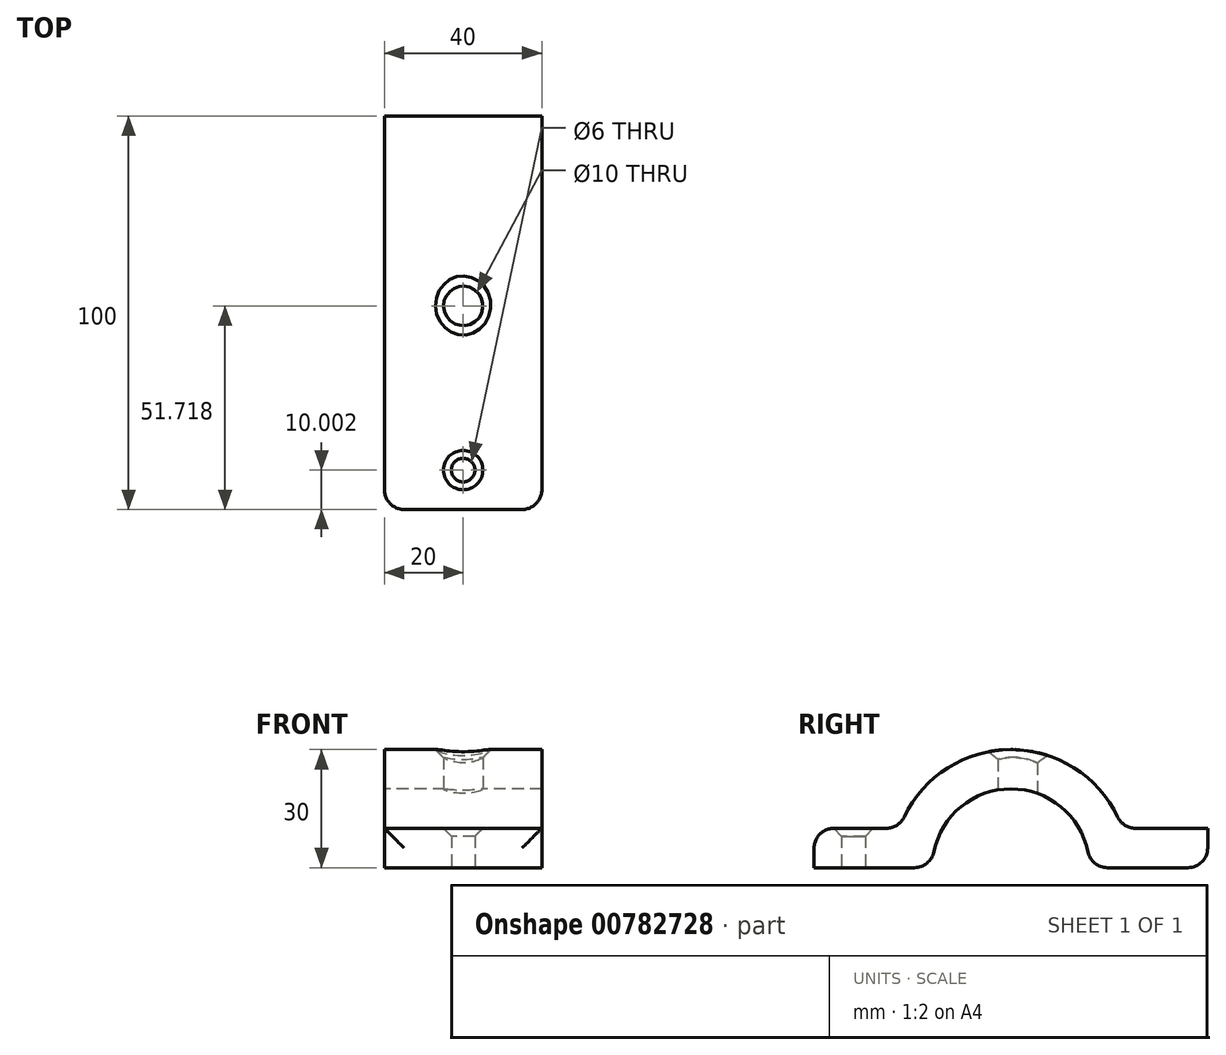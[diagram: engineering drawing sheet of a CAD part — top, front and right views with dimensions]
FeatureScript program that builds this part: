
annotation { "Feature Type Name" : "Feature", "Feature Type Description" : "" }
export const myFeature = defineFeature(function(context is Context, id is Id, definition is map)
    precondition{}
    {
        {
            var Q0;
            Q0=qCreatedBy(makeId("Right.planeOp"),FACE);
            var sketch = newSketch(context, id + "F0", { "sketchPlane" : qUnion([Q0])});
            skLineSegment(sketch, "E0.bottom", {"start": v(-60.57, 10) * mm, "end": v(39.43, 10) * mm});
            skLineSegment(sketch, "E0.top", {"start": v(-60.57, 0) * mm, "end": v(39.43, 0) * mm});
            skLineSegment(sketch, "E0.left", {"start": v(-60.57, 10) * mm, "end": v(-60.57, 0) * mm});
            skLineSegment(sketch, "E0.right", {"start": v(39.43, 10) * mm, "end": v(39.43, 0) * mm});
            skLineSegment(sketch, "E1.bottom", {"start": v(39.43, 10) * mm, "end": v(26.15, 10) * mm});
            skLineSegment(sketch, "E1.top", {"start": v(39.43, 50) * mm, "end": v(26.15, 50) * mm});
            skLineSegment(sketch, "E1.left", {"start": v(39.43, 10) * mm, "end": v(39.43, 50) * mm});
            skLineSegment(sketch, "E1.right", {"start": v(26.15, 10) * mm, "end": v(26.15, 50) * mm});
            skPoint(sketch, "E2", {"position": v(-10.57, 0) * mm});
            skCircle(sketch, "E3", {"center": v(-10.57, 0) * mm, "radius": 30 * mm});
            skCircle(sketch, "E4", {"center": v(-10.57, 0) * mm, "radius": 20 * mm});
            skSolve(sketch);
        }
        {
            var Q0;
            {var subQ0=sQuery(id+"F0.wireOp",EDGE,"E0.left");Q0=makeQuery(id+"F0.imprint","IMPRINT",FACE,{"disambiguationData":[TD([[makeQuery(id+"F0.imprint","IMPRINT",EDGE,{"derivedFrom":subQ0}),1.0]])]});}
            var Q1;
            {var subQ0=sQuery(id+"F0.wireOp",EDGE,"E3");var subQ1=sQuery(id+"F0.wireOp",EDGE,"E0.bottom");var subQ2=makeQuery(id+"F0.imprint","INTERSECT",VERTEX,{"disambiguationData":[OD(0.0)],"derivedFrom":[subQ1,subQ0]});Q1=makeQuery(id+"F0.imprint","IMPRINT",FACE,{"disambiguationData":[TD([[makeQuery(id+"F0.imprint","IMPRINT",EDGE,{"disambiguationData":[TD([[subQ2,-1.0]])],"derivedFrom":subQ1}),-1.0]])]});}
            var Q2;
            {var subQ0=sQuery(id+"F0.wireOp",EDGE,"E3");var subQ1=sQuery(id+"F0.wireOp",EDGE,"E0.bottom");var subQ2=makeQuery(id+"F0.imprint","INTERSECT",VERTEX,{"disambiguationData":[OD(0.0)],"derivedFrom":[subQ1,subQ0]});Q2=makeQuery(id+"F0.imprint","IMPRINT",FACE,{"disambiguationData":[TD([[makeQuery(id+"F0.imprint","IMPRINT",EDGE,{"disambiguationData":[TD([[subQ2,-1.0]])],"derivedFrom":subQ1}),1.0]])]});}
            var Q3;
            {var subQ0=sQuery(id+"F0.wireOp",EDGE,"E3");var subQ1=sQuery(id+"F0.wireOp",EDGE,"E0.bottom");var subQ2=makeQuery(id+"F0.imprint","INTERSECT",VERTEX,{"disambiguationData":[OD(1.0)],"derivedFrom":[subQ1,subQ0]});Q3=makeQuery(id+"F0.imprint","IMPRINT",FACE,{"disambiguationData":[TD([[makeQuery(id+"F0.imprint","IMPRINT",EDGE,{"disambiguationData":[TD([[subQ2,1.0]])],"derivedFrom":subQ1}),-1.0]])]});}
            var Q4;
            {var subQ1=sQuery(id+"F0.wireOp",EDGE,"E0.right");Q4=makeQuery(id+"F0.imprint","IMPRINT",FACE,{"disambiguationData":[TD([[makeQuery(id+"F0.imprint","IMPRINT",EDGE,{"derivedFrom":subQ1}),-1.0]])]});}
            var Q5;
            Q5=makeQuery(id+"F0.imprint","IMPRINT",FACE,{"disambiguationData":[TD([[makeQuery(id+"F0.imprint","IMPRINT",EDGE,{"derivedFrom":sQuery(id+"F0.wireOp",EDGE,"E1.bottom")}),-1.0]])]});
            extrude(context, id + "F1", {"entities" : qUnion([Q0, Q1, Q2, Q3, Q4, Q5]), "endBound" : BoundingType.SYMMETRIC, "depth" : 40 * mm, "offsetDistance" : 25 * mm});
        }
        {
            var Q0;
            Q0=makeQuery(id+"F1.opExtrude","SWEPT_FACE",FACE,{"disambiguationData":[OSD([sQuery(id+"F0.wireOp",EDGE,"E0.right"),sQuery(id+"F0.wireOp",EDGE,"E1.left")])]});
            var sketch = newSketch(context, id + "F2", { "sketchPlane" : qUnion([Q0])});
            skLineSegment(sketch, "E5.bottom", {"start": v(-5, 50) * mm, "end": v(5, 50) * mm});
            skLineSegment(sketch, "E5.top", {"start": v(-3, 35) * mm, "end": v(3, 35) * mm});
            skLineSegment(sketch, "E5.left", {"start": v(-5, 50) * mm, "end": v(-5, 37) * mm});
            skLineSegment(sketch, "E5.right", {"start": v(5, 50) * mm, "end": v(5, 37) * mm});
            skPoint(sketch, "E6.visualSharp", {"position": v(5, 35) * mm});
            skArc(sketch, "E6.filletArc", {"start": v(3, 35) * mm, "mid": v(4.41, 35.59) * mm, "end": v(5, 37) * mm});
            skPoint(sketch, "E7.visualSharp", {"position": v(-5, 35) * mm});
            skArc(sketch, "E7.filletArc", {"start": v(-5, 37) * mm, "mid": v(-4.41, 35.59) * mm, "end": v(-3, 35) * mm});
            skPoint(sketch, "E8", {"position": v(0, 50) * mm});
            skPoint(sketch, "E9", {"position": v(0, 25) * mm});
            skCircle(sketch, "E10", {"center": v(0, 25) * mm, "radius": 3 * mm});
            skSolve(sketch);
        }
        {
            var Q0;
            Q0=makeQuery(id+"F2.imprint","IMPRINT",FACE,{"disambiguationData":[TD([[makeQuery(id+"F2.imprint","IMPRINT",EDGE,{"derivedFrom":sQuery(id+"F2.wireOp",EDGE,"E5.bottom")}),-1.0]])]});
            extrude(context, id + "F3", {"entities" : qUnion([Q0]), "operationType" : NewBodyOperationType.REMOVE, "oppositeDirection" : true, "depth" : 15.6 * mm, "offsetDistance" : 25 * mm});
        }
        {
            var Q0;
            Q0=qCreatedBy(makeId("Top.planeOp"),FACE);
            var sketch = newSketch(context, id + "F4", { "sketchPlane" : qUnion([Q0])});
            skCircle(sketch, "E11", {"center": v(0, -50.57) * mm, "radius": 3 * mm});
            skCircle(sketch, "E12", {"center": v(0, -8.85) * mm, "radius": 5 * mm});
            skSolve(sketch);
        }
        {
            var Q0;
            Q0=makeQuery(id+"F4.imprint","IMPRINT",FACE,{"disambiguationData":[TD([[makeQuery(id+"F4.imprint","IMPRINT",EDGE,{"derivedFrom":sQuery(id+"F4.wireOp",EDGE,"E11")}),1.0]])]});
            var Q1;
            Q1=makeQuery(id+"F4.imprint","IMPRINT",FACE,{"disambiguationData":[TD([[makeQuery(id+"F4.imprint","IMPRINT",EDGE,{"derivedFrom":sQuery(id+"F4.wireOp",EDGE,"E12")}),1.0]])]});
            extrude(context, id + "F5", {"entities" : qUnion([Q0, Q1]), "operationType" : NewBodyOperationType.REMOVE, "depth" : 34.2 * mm, "offsetDistance" : 25 * mm});
        }
        {
            var Q0;
            Q0=makeQuery(id+"F1.opExtrude","CAP_EDGE",EDGE,{"disambiguationData":[OSD([sQuery(id+"F0.wireOp",EDGE,"E1.top")])],"isStart":true});
            var Q1;
            Q1=makeQuery(id+"F1.opExtrude","CAP_EDGE",EDGE,{"disambiguationData":[OSD([sQuery(id+"F0.wireOp",EDGE,"E1.top")])],"isStart":false});
            var Q2;
            Q2=makeQuery(id+"F1.opExtrude","CAP_EDGE",EDGE,{"disambiguationData":[OSD([sQuery(id+"F0.wireOp",EDGE,"E0.left")])],"isStart":false});
            var Q3;
            Q3=makeQuery(id+"F1.opExtrude","CAP_EDGE",EDGE,{"disambiguationData":[OSD([sQuery(id+"F0.wireOp",EDGE,"E0.left")])],"isStart":true});
            var Q4;
            {var subQ0=sQuery(id+"F0.wireOp",EDGE,"E4");var subQ1=sQuery(id+"F0.wireOp",EDGE,"E0.top");Q4=makeQuery(id+"F1.opExtrude","SWEPT_EDGE",EDGE,{"disambiguationData":[OSD([subQ1,subQ0]),TDD([makeQuery(id+"F0.imprint","INTERSECT",VERTEX,{"disambiguationData":[OD(1.0)],"derivedFrom":[subQ1,subQ0]})])]});}
            var Q5;
            {var subQ0=sQuery(id+"F0.wireOp",EDGE,"E4");var subQ1=sQuery(id+"F0.wireOp",EDGE,"E0.top");Q5=makeQuery(id+"F1.opExtrude","SWEPT_EDGE",EDGE,{"disambiguationData":[OSD([subQ1,subQ0]),TDD([makeQuery(id+"F0.imprint","INTERSECT",VERTEX,{"disambiguationData":[OD(0.0)],"derivedFrom":[subQ1,subQ0]})])]});}
            var Q6;
            {var subQ0=sQuery(id+"F0.wireOp",EDGE,"E3");var subQ1=sQuery(id+"F0.wireOp",EDGE,"E0.bottom");Q6=makeQuery(id+"F1.opExtrude","SWEPT_EDGE",EDGE,{"disambiguationData":[OSD([subQ1,subQ0]),TDD([makeQuery(id+"F0.imprint","INTERSECT",VERTEX,{"disambiguationData":[OD(0.0)],"derivedFrom":[subQ1,subQ0]})])]});}
            var Q7;
            {var subQ0=sQuery(id+"F0.wireOp",EDGE,"E3");var subQ1=sQuery(id+"F0.wireOp",EDGE,"E0.bottom");Q7=makeQuery(id+"F1.opExtrude","SWEPT_EDGE",EDGE,{"disambiguationData":[OSD([subQ1,subQ0]),TDD([makeQuery(id+"F0.imprint","INTERSECT",VERTEX,{"disambiguationData":[OD(1.0)],"derivedFrom":[subQ1,subQ0]})])]});}
            var Q8;
            Q8=makeQuery(id+"F1.opExtrude","SWEPT_EDGE",EDGE,{"disambiguationData":[OSD([sQuery(id+"F0.wireOp",EDGE,"E0.bottom"),sQuery(id+"F0.wireOp",EDGE,"E1.bottom"),sQuery(id+"F0.wireOp",EDGE,"E1.right")])]});
            var Q9;
            Q9=makeQuery(id+"F1.opExtrude","SWEPT_EDGE",EDGE,{"disambiguationData":[OSD([sQuery(id+"F0.wireOp",EDGE,"E0.top"),sQuery(id+"F0.wireOp",EDGE,"E0.right")])]});
            fillet(context, id + "F6", {"entities" : qUnion([Q0, Q1, Q2, Q3, Q4, Q5, Q6, Q7, Q8, Q9]), "radius" : 5 * mm, "tangentPropagation" : true, "allowEdgeOverflow" : false});
        }
        {
            var Q0;
            {var subQ0=sQuery(id+"F0.wireOp",EDGE,"E0.bottom");Q0=makeQuery(id+"F5.boolean.opBoolean","INTERSECT",EDGE,{"derivedFrom":[makeQuery(id+"F1.opExtrude","SWEPT_FACE",FACE,{"disambiguationData":[OSD([subQ0]),TDD([makeQuery(id+"F0.imprint","IMPRINT",EDGE,{"disambiguationData":[TD([[makeQuery(id+"F0.imprint","INTERSECT",VERTEX,{"derivedFrom":[subQ0,sQuery(id+"F0.wireOp",EDGE,"E0.left")]}),-1.0]])],"derivedFrom":subQ0})])]}),makeQuery(id+"F5.opExtrude","SWEPT_FACE",FACE,{"disambiguationData":[OSD([sQuery(id+"F4.wireOp",EDGE,"E11")])]})]});}
            chamfer(context, id + "F7", {"entities" : qUnion([Q0]), "width" : 2 * mm, "tangentPropagation" : true});
        }
        {
            var Q0;
            Q0=makeQuery(id+"F5.boolean.opBoolean","INTERSECT",EDGE,{"derivedFrom":[makeQuery(id+"F1.opExtrude","SWEPT_FACE",FACE,{"disambiguationData":[OSD([sQuery(id+"F0.wireOp",EDGE,"E3")])]}),makeQuery(id+"F5.opExtrude","SWEPT_FACE",FACE,{"disambiguationData":[OSD([sQuery(id+"F4.wireOp",EDGE,"E12")])]})]});
            chamfer(context, id + "F8", {"entities" : qUnion([Q0]), "width" : 2 * mm, "tangentPropagation" : true});
        }
        {
            var Q0;
            Q0=makeQuery(id+"F2.imprint","IMPRINT",FACE,{"disambiguationData":[TD([[makeQuery(id+"F2.imprint","IMPRINT",EDGE,{"derivedFrom":sQuery(id+"F2.wireOp",EDGE,"E10")}),1.0]])]});
            extrude(context, id + "F9", {"entities" : qUnion([Q0]), "operationType" : NewBodyOperationType.REMOVE, "oppositeDirection" : true, "depth" : 17.7 * mm, "offsetDistance" : 25 * mm});
        }
    });
